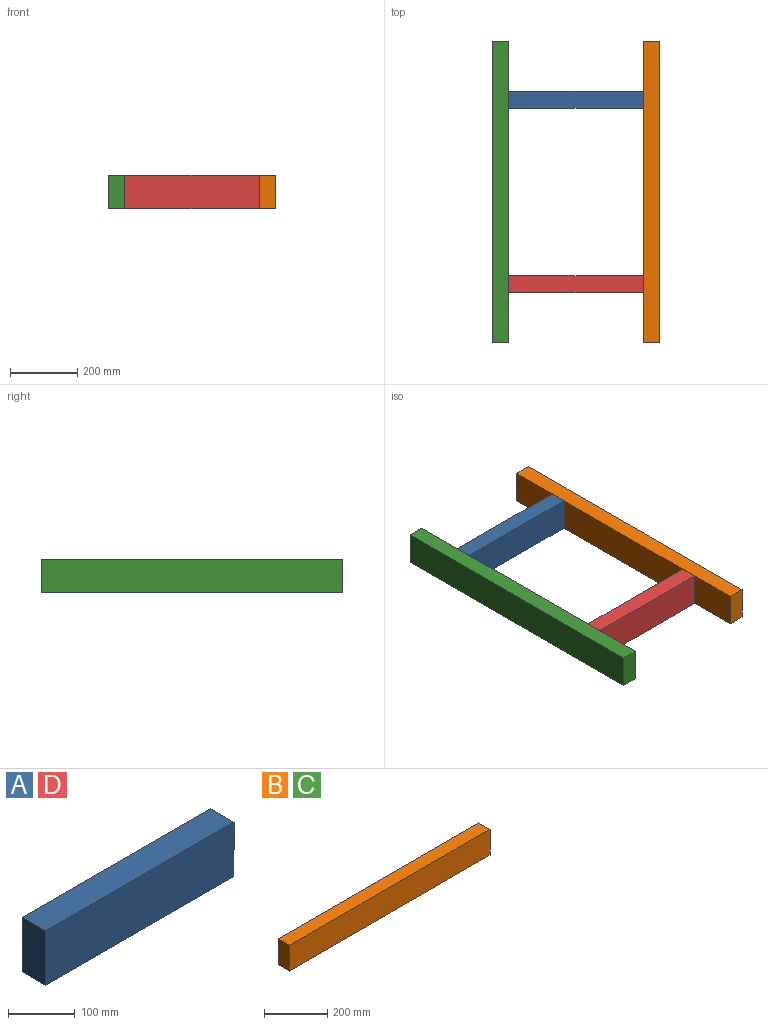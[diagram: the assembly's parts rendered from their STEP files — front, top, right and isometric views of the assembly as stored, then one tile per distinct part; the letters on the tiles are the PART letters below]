
ASSEMBLY  parts=4 mates=3
PART A: 6 faces, bbox 400x50x100 mm
  f0: plane 400x100mm, normal (0,-1,0), area 40000mm2, adj f1,f3,f4,f5
  f1: plane 400x50mm, normal (0,0,-1), area 20000mm2, adj f0,f2,f4,f5
  f2: plane 400x100mm, normal (0,1,0), area 40000mm2, adj f1,f3,f4,f5
  f3: plane 400x50mm, normal (0,0,1), area 20000mm2, adj f0,f2,f4,f5
  f4: plane 100x50mm, normal (1,0,0), area 5000mm2, adj f0,f1,f2,f3
  f5: plane 100x50mm, normal (-1,0,0), area 5000mm2, adj f0,f1,f2,f3
PART B: 6 faces, bbox 900x50x100 mm
  f0: plane 900x100mm, normal (0,-1,0), area 90000mm2, adj f1,f3,f4,f5
  f1: plane 900x50mm, normal (0,0,-1), area 45000mm2, adj f0,f2,f4,f5
  f2: plane 900x100mm, normal (0,1,0), area 90000mm2, adj f1,f3,f4,f5
  f3: plane 900x50mm, normal (0,0,1), area 45000mm2, adj f0,f2,f4,f5
  f4: plane 100x50mm, normal (1,0,0), area 5000mm2, adj f0,f1,f2,f3
  f5: plane 100x50mm, normal (-1,0,0), area 5000mm2, adj f0,f1,f2,f3
PART C: same geometry as B
PART D: same geometry as A
PLACE A t=(385.37,852.87,-65.15)mm
PLACE B rot(axis=(0,0,-1),90deg) t=(785.37,1052.87,-65.15)mm
PLACE C rot(axis=(0,0,-1),90deg) t=(335.37,1052.87,-65.15)mm
PLACE D t=(385.37,302.87,-65.15)mm
MATE fastened A.f3 <-> C.f3  axis (0,0,1) through (385.37,902.87,34.85)mm
MATE fastened C.f3 <-> D.f3  axis (0,0,1) through (385.37,152.87,34.85)mm
MATE fastened B.f3 <-> D.f3  axis (0,0,1) through (785.37,152.87,34.85)mm
